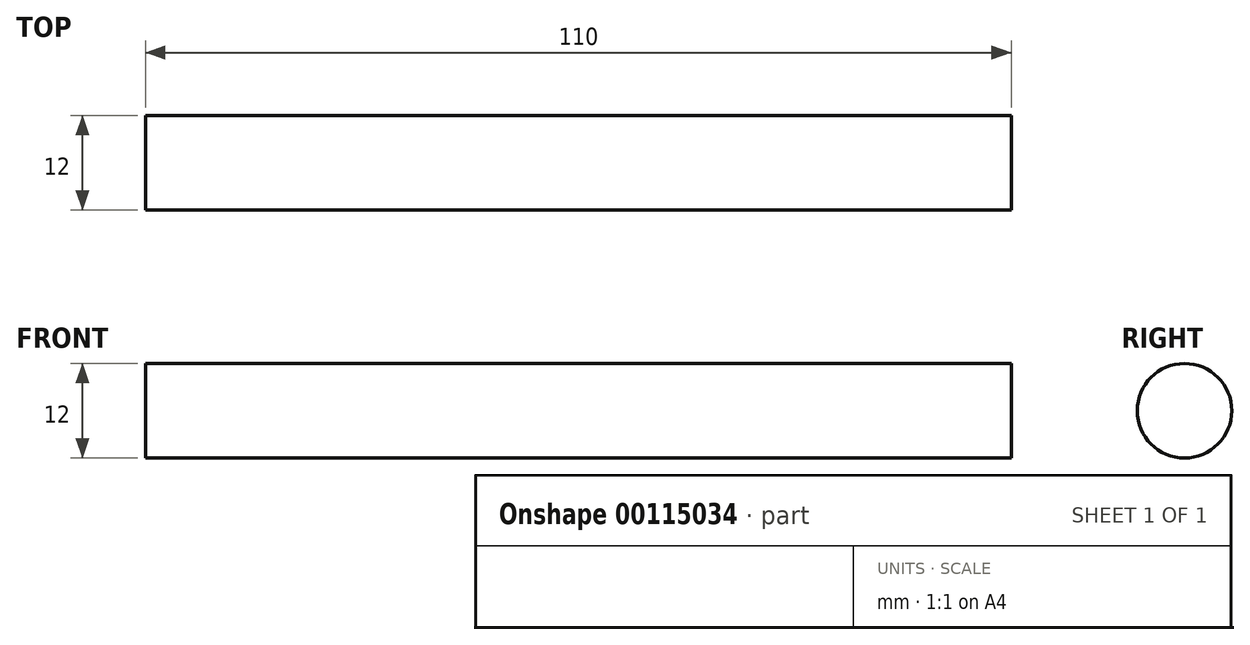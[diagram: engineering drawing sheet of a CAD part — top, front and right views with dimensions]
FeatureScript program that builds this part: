
annotation { "Feature Type Name" : "Feature", "Feature Type Description" : "" }
export const myFeature = defineFeature(function(context is Context, id is Id, definition is map)
    precondition{}
    {
        {
            var Q0;
            Q0=qCreatedBy(makeId("Front.planeOp"),FACE);
            var sketch = newSketch(context, id + "F0", { "sketchPlane" : qUnion([Q0])});
            skLineSegment(sketch, "E0.bottom", {"start": v(0, 0) * mm, "end": v(-55, 0) * mm});
            skLineSegment(sketch, "E0.top", {"start": v(0, 6) * mm, "end": v(-55, 6) * mm});
            skLineSegment(sketch, "E0.left", {"start": v(0, 0) * mm, "end": v(0, 6) * mm});
            skLineSegment(sketch, "E0.right", {"start": v(-55, 0) * mm, "end": v(-55, 6) * mm});
            skLineSegment(sketch, "E1.MirrorCS", {"start": v(0, 6) * mm, "end": v(55, 6) * mm});
            skLineSegment(sketch, "E2.MirrorCS", {"start": v(55, 0) * mm, "end": v(55, 6) * mm});
            skLineSegment(sketch, "E3.MirrorCS", {"start": v(0, 0) * mm, "end": v(55, 0) * mm});
            skSolve(sketch);
        }
        {
            var Q0;
            Q0 = qSketchRegion(id + "F0", true);
            var Q1;
            Q1=sQuery(id+"F0.wireOp",EDGE,"E0.bottom");
            revolve(context, id + "F1", {"entities" : qUnion([Q0]), "axis" : qUnion([Q1]), "revolveType" : RevolveType.FULL});
        }
    });
